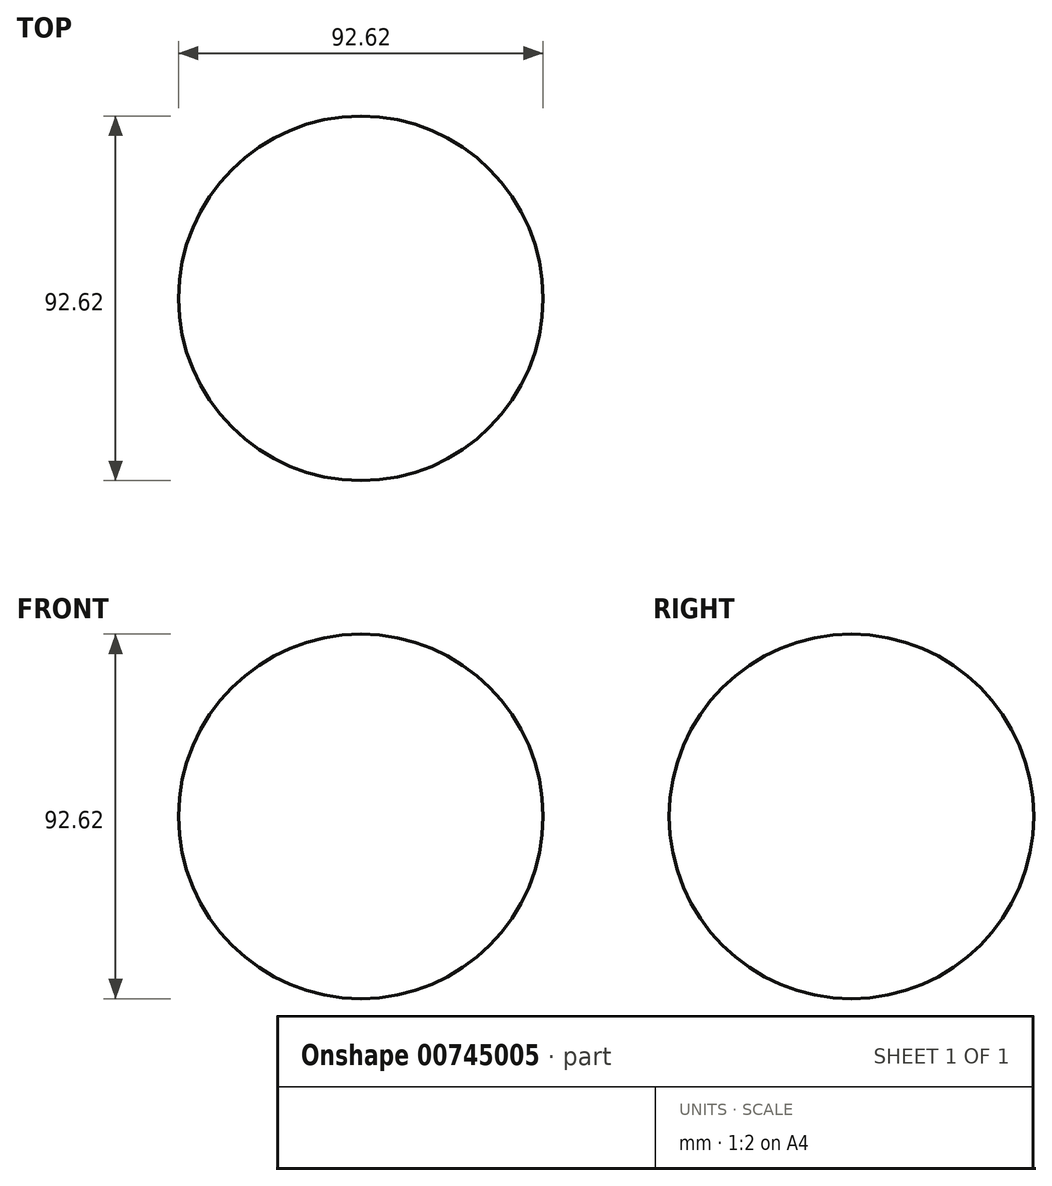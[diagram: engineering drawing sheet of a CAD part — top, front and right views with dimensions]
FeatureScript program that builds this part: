
annotation { "Feature Type Name" : "Feature", "Feature Type Description" : "" }
export const myFeature = defineFeature(function(context is Context, id is Id, definition is map)
    precondition{}
    {
        {
            var Q0;
            Q0=qCreatedBy(makeId("Front.planeOp"),FACE);
            var sketch = newSketch(context, id + "F0", { "sketchPlane" : qUnion([Q0])});
            skArc(sketch, "E0", {"start": v(0, 46.3) * mm, "mid": v(-46.3, 0) * mm, "end": v(0, -46.3) * mm});
            skLineSegment(sketch, "E1", {"start": v(0, 46.3) * mm, "end": v(0, -46.3) * mm});
            skPoint(sketch, "E2.orphan", {"position": v(0, 51.9) * mm});
            skSolve(sketch);
        }
        {
            var Q0;
            Q0 = qSketchRegion(id + "F0", true);
            var Q1;
            Q1=sQuery(id+"F0.wireOp",EDGE,"E1");
            revolve(context, id + "F1", {"surfaceOperationType" : NewSurfaceOperationType.NEW, "entities" : qUnion([Q0]), "axis" : qUnion([Q1]), "revolveType" : RevolveType.FULL});
        }
    });
